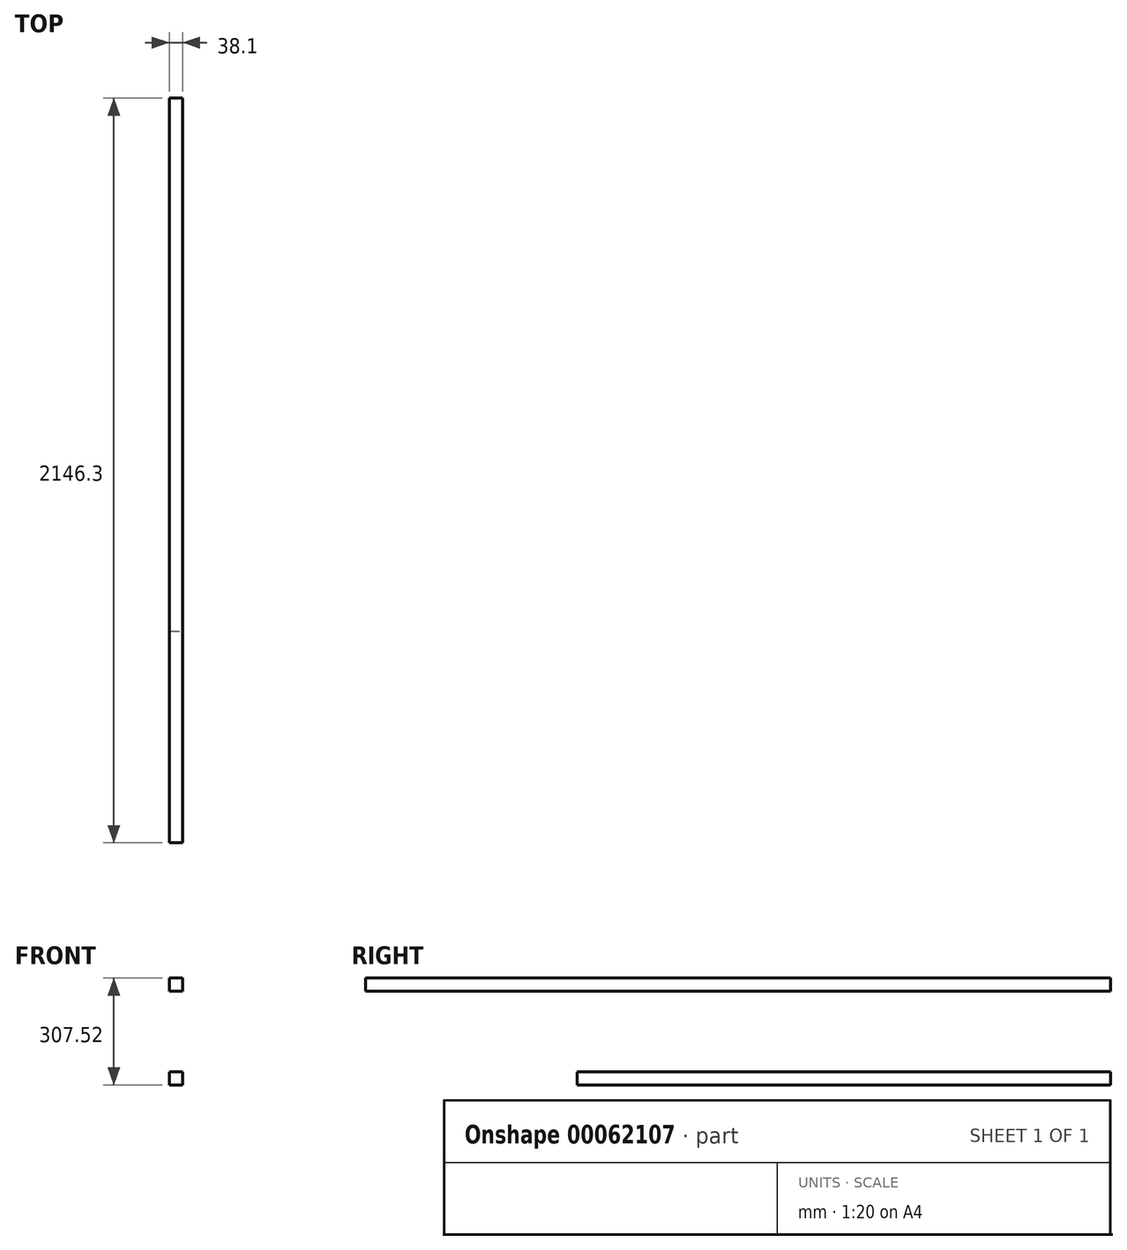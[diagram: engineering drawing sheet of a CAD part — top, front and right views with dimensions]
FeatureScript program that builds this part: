
annotation { "Feature Type Name" : "Feature", "Feature Type Description" : "" }
export const myFeature = defineFeature(function(context is Context, id is Id, definition is map)
    precondition{}
    {
        {
            var Q0;
            Q0=qCreatedBy(makeId("Front.planeOp"),FACE);
            var sketch = newSketch(context, id + "F0", { "sketchPlane" : qUnion([Q0])});
            skLineSegment(sketch, "E0", {"start": v(0, 0) * mm, "end": v(0, 28.57) * mm, "construction": true});
            skLineSegment(sketch, "E1", {"start": v(0, 0) * mm, "end": v(31.75, 0) * mm, "construction": true});
            skLineSegment(sketch, "E2.bottom", {"start": v(-19.05, 19.05) * mm, "end": v(19.05, 19.05) * mm});
            skLineSegment(sketch, "E2.top", {"start": v(-19.05, -19.05) * mm, "end": v(19.05, -19.05) * mm});
            skLineSegment(sketch, "E2.left", {"start": v(-19.05, 19.05) * mm, "end": v(-19.05, -19.05) * mm});
            skLineSegment(sketch, "E2.right", {"start": v(19.05, 19.05) * mm, "end": v(19.05, -19.05) * mm});
            skSolve(sketch);
        }
        {
            var Q0;
            Q0=makeQuery(id+"F0.imprint","IMPRINT",FACE,{"disambiguationData":[TD([[makeQuery(id+"F0.imprint","IMPRINT",EDGE,{"derivedFrom":sQuery(id+"F0.wireOp",EDGE,"E2.bottom")}),-1.0]])]});
            extrude(context, id + "F1", {"entities" : qUnion([Q0]), "depth" : 1536.7 * mm});
        }
        {
            var Q0;
            Q0=makeQuery(id+"F1.opExtrude","SWEPT_BODY",BODY,{"disambiguationData":[OSD([sQuery(id+"F0.wireOp",EDGE,"E2.bottom"),sQuery(id+"F0.wireOp",EDGE,"E2.top"),sQuery(id+"F0.wireOp",EDGE,"E2.left"),sQuery(id+"F0.wireOp",EDGE,"E2.right")])]});
            transform(context, id + "F2", {"entities" : qUnion([Q0]), "transformType" : TransformType.TRANSLATION_3D, "dx" : 0 * mm, "dy" : 0 * mm, "dz" : 269.42 * mm, "makeCopy" : true});
        }
        {
            var Q0;
            Q0=makeQuery(id+"F2.opPattern","COPY",FACE,{"derivedFrom":makeQuery(id+"F1.opExtrude","CAP_FACE",FACE,{"disambiguationData":[OSD([sQuery(id+"F0.wireOp",EDGE,"E2.bottom"),sQuery(id+"F0.wireOp",EDGE,"E2.top"),sQuery(id+"F0.wireOp",EDGE,"E2.left"),sQuery(id+"F0.wireOp",EDGE,"E2.right")])],"isStart":false}),"instanceName":"1"});
            extrude(context, id + "F3", {"entities" : qUnion([Q0]), "operationType" : NewBodyOperationType.ADD, "depth" : 609.6 * mm});
        }
    });
